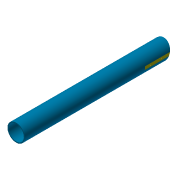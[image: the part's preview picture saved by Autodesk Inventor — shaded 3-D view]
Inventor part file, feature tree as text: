
AUTODESK INVENTOR PART (.ipt)
format: ipt  version: 2016 (Build 200138000, 138)  size: 125,440 bytes
history: native  units: in
note: dims shown in document units (in); Inventor stores cm internally (conversion verified against a paired STEP export)
features: sketch x6, extrude x3, plane x3, hole x1
ambient origin geometry x8: Origin, YZ Plane, XZ Plane, XY Plane, X Axis, Y Axis, Z Axis, Center Point
bodies: Solid1 (feature_tree)
feature tree (13):
  extrude  "tube"  Depth=0.1417in
  sketch  "Sketch15"  dims[d3=21.1024in d4=0.0in d66=1.2205in]
  plane  "Work Plane6"
  plane  "Work Plane7"
  extrude  "flatFaceYellow"  Depth=1.2205in
  sketch  "Sketch21"  dims[d69=1.0in d70=0.0in d86=0.1264in]
  plane  "Work Plane8"
  extrude  "angledEnd"  Depth=3.937in
  hole  "Hole3"  [1 undecoded]
  sketch  "Sketch1"  dims[d0=2.4803in d2=0.1417in]
  sketch  "Sketch19"  dims[d67=0.7874in d68=3.937in]
  sketch  "Sketch22"  dims[d87=1.0in d88=0.0in]
  sketch  "Sketch23"  dims[d89=3.1496in d90=0.7874in d92=1.5748in d93=0.3937in d95=1.0in d97=0.0787in d98=0.75in d99=0.375in d100=0.25in d101=0.5635in d102=1.0in d103=0.8108in]
note: 1 required parameter value undecoded (feature->parameter linkage not recoverable at this tier; creation-order binding heuristic only, values carry confidence <= 0.55)
